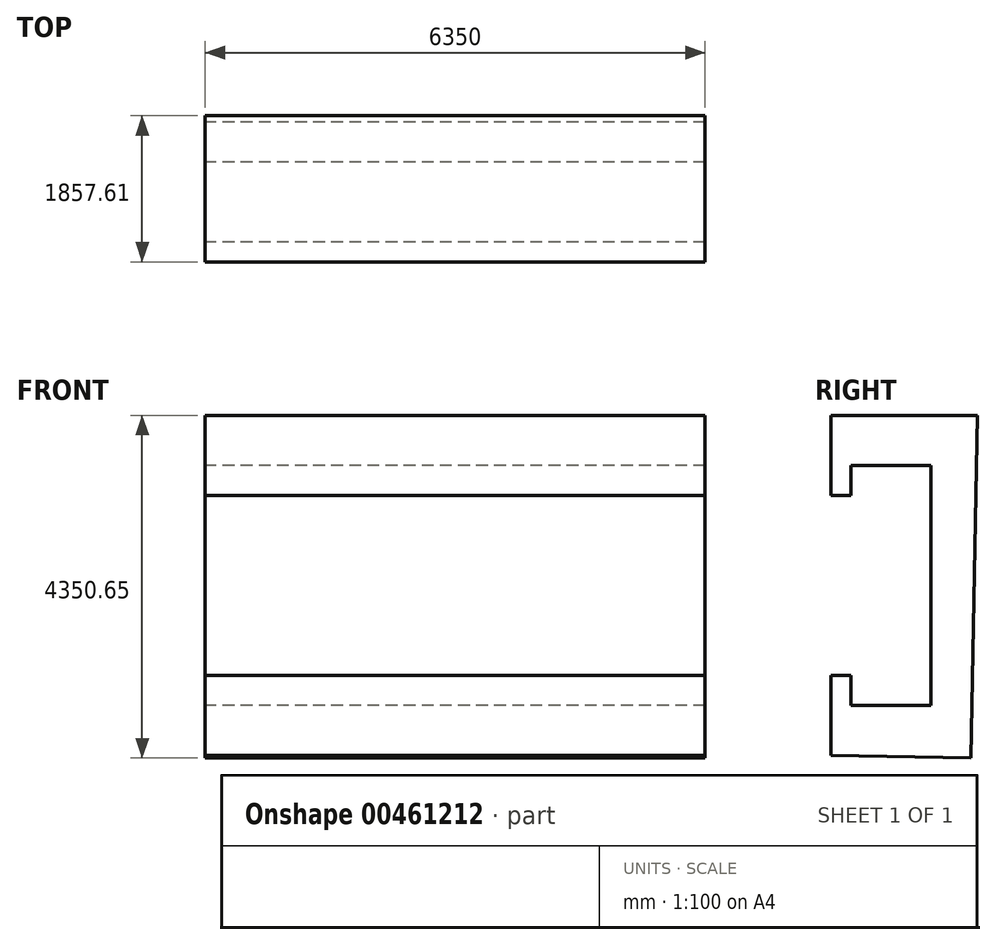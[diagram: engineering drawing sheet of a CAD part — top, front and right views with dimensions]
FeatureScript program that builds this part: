
annotation { "Feature Type Name" : "Feature", "Feature Type Description" : "" }
export const myFeature = defineFeature(function(context is Context, id is Id, definition is map)
    precondition{}
    {
        {
            var Q0;
            Q0=qCreatedBy(makeId("Right.planeOp"),FACE);
            var sketch = newSketch(context, id + "F0", { "sketchPlane" : qUnion([Q0])});
            skLineSegment(sketch, "E0", {"start": v(0, 0) * mm, "end": v(0, 1524) * mm});
            skLineSegment(sketch, "E1", {"start": v(0, 0) * mm, "end": v(0, -1524) * mm});
            skLineSegment(sketch, "E2", {"start": v(0, 1524) * mm, "end": v(-1016, 1524) * mm});
            skLineSegment(sketch, "E3", {"start": v(-1016, 1524) * mm, "end": v(-1016, 1143) * mm});
            skLineSegment(sketch, "E4", {"start": v(-1016, 1143) * mm, "end": v(-1270, 1143) * mm});
            skLineSegment(sketch, "E5", {"start": v(-1270, 1143) * mm, "end": v(-1270, 2159) * mm});
            skLineSegment(sketch, "E6", {"start": v(-1270, 2159) * mm, "end": v(587.61, 2159) * mm});
            skLineSegment(sketch, "E7", {"start": v(587.61, 2159) * mm, "end": v(507.7, -2191.65) * mm});
            skLineSegment(sketch, "E8", {"start": v(507.7, -2191.65) * mm, "end": v(-1270, -2159) * mm});
            skLineSegment(sketch, "E9", {"start": v(-1270, -2159) * mm, "end": v(-1270, -1143) * mm});
            skLineSegment(sketch, "E10", {"start": v(-1270, -1143) * mm, "end": v(-1016, -1143) * mm});
            skLineSegment(sketch, "E11", {"start": v(-1016, -1143) * mm, "end": v(-1016, -1524) * mm});
            skLineSegment(sketch, "E12", {"start": v(-1016, -1524) * mm, "end": v(0, -1524) * mm});
            skSolve(sketch);
        }
        {
            var Q0;
            Q0 = qSketchRegion(id + "F0", true);
            extrude(context, id + "F1", {"entities" : qUnion([Q0]), "depth" : 6350 * mm});
        }
    });
